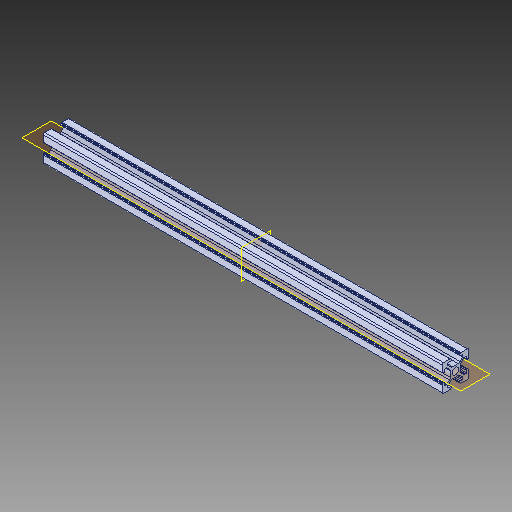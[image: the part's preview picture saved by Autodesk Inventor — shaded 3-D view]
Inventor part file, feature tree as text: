
AUTODESK INVENTOR PART (.ipt)
format: ipt  version: 2018 (Build 220112000, 112)  size: 373,760 bytes
history: native  units: in
note: dims shown in document units (in); Inventor stores cm internally (conversion verified against a paired STEP export)
features: extrude x1, plane x1, sketch x1, projected_geometry x1, fillet x1
ambient origin geometry x8: Origin, YZ Plane, XZ Plane, XY Plane, X Axis, Y Axis, Z Axis, Center Point
bodies: Solid1 (feature_tree)
feature tree (5):
  extrude  "Extrusion2"  [1 undecoded]
  plane  "Work Plane1"
  sketch  "Sketch3"  dims[d2=7.874in d3=0.0in]
  projected_geometry  "Projected Loop2"
  fillet  "Fillet5"  [1 undecoded]
note: 2 required parameter values undecoded (feature->parameter linkage not recoverable at this tier; creation-order binding heuristic only, values carry confidence <= 0.55)
